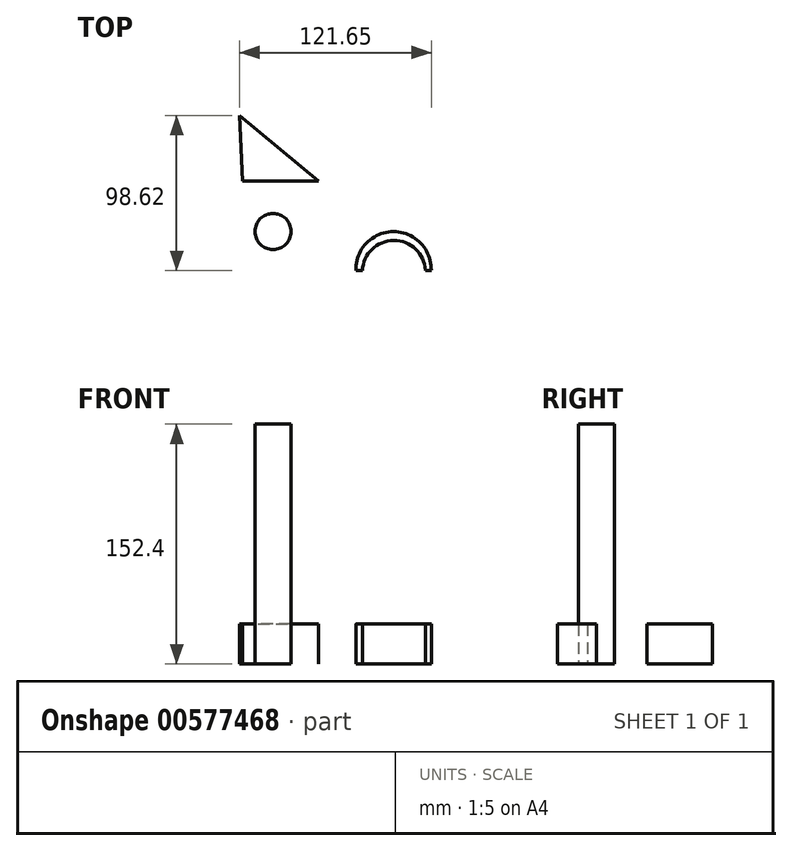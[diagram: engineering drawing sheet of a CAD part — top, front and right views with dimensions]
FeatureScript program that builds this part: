
annotation { "Feature Type Name" : "Feature", "Feature Type Description" : "" }
export const myFeature = defineFeature(function(context is Context, id is Id, definition is map)
    precondition{}
    {
        {
            var Q0;
            Q0=qCreatedBy(makeId("Top.planeOp"),FACE);
            var sketch = newSketch(context, id + "F0", { "sketchPlane" : qUnion([Q0])});
            skLineSegment(sketch, "E0", {"start": v(-63.26, 54.9) * mm, "end": v(-13.26, 13.26) * mm});
            skLineSegment(sketch, "E1", {"start": v(-13.26, 13.26) * mm, "end": v(-61.4, 13.26) * mm});
            skLineSegment(sketch, "E2", {"start": v(-61.4, 13.26) * mm, "end": v(-63.26, 54.9) * mm});
            skSolve(sketch);
        }
        {
            var Q0;
            Q0=makeQuery(id+"F0.imprint","IMPRINT",FACE,{"disambiguationData":[TD([[makeQuery(id+"F0.imprint","IMPRINT",EDGE,{"derivedFrom":sQuery(id+"F0.wireOp",EDGE,"E0")}),-1.0]])]});
            extrude(context, id + "F1", {"entities" : qUnion([Q0]), "depth" : 25.4 * mm, "offsetDistance" : 25.4 * mm});
        }
        {
            var Q0;
            Q0=qCreatedBy(makeId("Top.planeOp"),FACE);
            var sketch = newSketch(context, id + "F2", { "sketchPlane" : qUnion([Q0])});
            skCircle(sketch, "E3", {"center": v(-42.1, -18.84) * mm, "radius": 11.46 * mm});
            skSolve(sketch);
        }
        {
            var Q0;
            Q0=makeQuery(id+"F2.imprint","IMPRINT",FACE,{"disambiguationData":[TD([[makeQuery(id+"F2.imprint","IMPRINT",EDGE,{"derivedFrom":sQuery(id+"F2.wireOp",EDGE,"E3")}),1.0]])]});
            extrude(context, id + "F3", {"entities" : qUnion([Q0]), "depth" : 152.4 * mm, "offsetDistance" : 25.4 * mm});
        }
        {
            var Q0;
            Q0=qCreatedBy(makeId("Top.planeOp"),FACE);
            var sketch = newSketch(context, id + "F4", { "sketchPlane" : qUnion([Q0])});
            skArc(sketch, "E4", {"start": v(54.66, -43.5) * mm, "mid": v(34.54, -24.57) * mm, "end": v(14.65, -43.73) * mm});
            skArc(sketch, "E5", {"start": v(58.38, -43.73) * mm, "mid": v(34.42, -18.94) * mm, "end": v(10.47, -43.73) * mm});
            skLineSegment(sketch, "E6", {"start": v(10.47, -43.73) * mm, "end": v(14.65, -43.73) * mm});
            skLineSegment(sketch, "E7", {"start": v(54.66, -43.5) * mm, "end": v(58.38, -43.73) * mm});
            skSolve(sketch);
        }
        {
            var Q0;
            Q0 = qSketchRegion(id + "F4", true);
            var Q1;
            Q1=makeQuery(id+"F4.imprint","IMPRINT",FACE,{"disambiguationData":[TD([[makeQuery(id+"F4.imprint","IMPRINT",EDGE,{"derivedFrom":sQuery(id+"F4.wireOp",EDGE,"E4")}),-1.0]])]});
            extrude(context, id + "F5", {"entities" : qUnion([Q0, Q1]), "depth" : 25.4 * mm, "offsetDistance" : 25.4 * mm});
        }
        {
            var Q0;
            Q0=makeQuery(id+"F3.opExtrude","CAP_FACE",FACE,{"disambiguationData":[OSD([sQuery(id+"F2.wireOp",EDGE,"E3")])],"isStart":false});
            var sketch = newSketch(context, id + "F6", { "sketchPlane" : qUnion([Q0])});
            skCircle(sketch, "E8", {"center": v(-42.1, -18.84) * mm, "radius": 6.85 * mm});
            skSolve(sketch);
        }
        {
            var Q0;
            Q0 = qSketchRegion(id + "F6", true);
            extrude(context, id + "F7", {"entities" : qUnion([Q0]), "operationType" : NewBodyOperationType.ADD, "oppositeDirection" : true, "depth" : 71.37 * mm, "offsetDistance" : 25.4 * mm});
        }
    });
